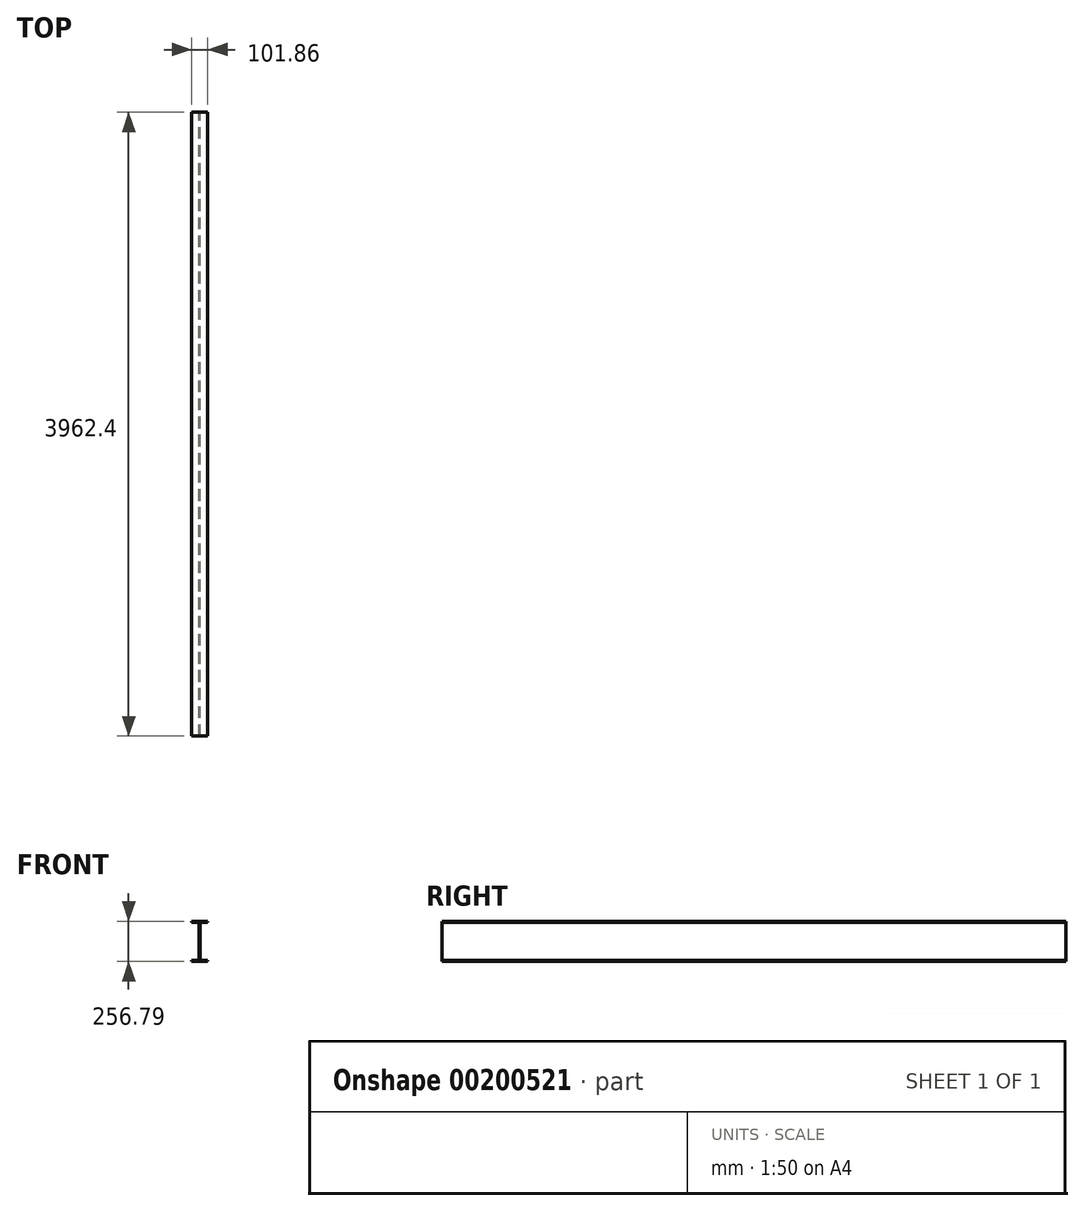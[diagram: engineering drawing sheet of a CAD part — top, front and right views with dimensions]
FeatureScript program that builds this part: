
annotation { "Feature Type Name" : "Feature", "Feature Type Description" : "" }
export const myFeature = defineFeature(function(context is Context, id is Id, definition is map)
    precondition{}
    {
        {
            var Q0;
            Q0=qCreatedBy(makeId("Front.planeOp"),FACE);
            var sketch = newSketch(context, id + "F0", { "sketchPlane" : qUnion([Q0])});
            skLineSegment(sketch, "E0", {"start": v(50.93, 0) * mm, "end": v(50.93, 8.38) * mm});
            skLineSegment(sketch, "E1", {"start": v(50.93, 8.38) * mm, "end": v(3.05, 8.38) * mm});
            skLineSegment(sketch, "E2", {"start": v(3.05, 8.38) * mm, "end": v(3.05, 248.41) * mm});
            skLineSegment(sketch, "E3", {"start": v(3.05, 248.41) * mm, "end": v(50.93, 248.41) * mm});
            skLineSegment(sketch, "E4", {"start": v(50.93, 248.41) * mm, "end": v(50.93, 256.8) * mm});
            skLineSegment(sketch, "E5", {"start": v(50.93, 256.8) * mm, "end": v(0, 256.8) * mm});
            skLineSegment(sketch, "E6", {"start": v(50.93, 0) * mm, "end": v(0, 0) * mm});
            skLineSegment(sketch, "E7", {"start": v(0, -24.07) * mm, "end": v(0, 108.97) * mm, "construction": true});
            skLineSegment(sketch, "E8.MirrorCS", {"start": v(-50.93, 248.41) * mm, "end": v(-50.93, 256.8) * mm});
            skLineSegment(sketch, "E9.MirrorCS", {"start": v(-50.93, 0) * mm, "end": v(-50.93, 8.38) * mm});
            skLineSegment(sketch, "E10.MirrorCS", {"start": v(-50.93, 8.38) * mm, "end": v(-3.05, 8.38) * mm});
            skLineSegment(sketch, "E11.MirrorCS", {"start": v(-3.05, 8.38) * mm, "end": v(-3.05, 248.41) * mm});
            skLineSegment(sketch, "E12.MirrorCS", {"start": v(-3.05, 248.41) * mm, "end": v(-50.93, 248.41) * mm});
            skLineSegment(sketch, "E13.MirrorCS", {"start": v(-50.93, 256.8) * mm, "end": v(0, 256.8) * mm});
            skLineSegment(sketch, "E14.MirrorCS", {"start": v(-50.93, 0) * mm, "end": v(0, 0) * mm});
            skSolve(sketch);
        }
        {
            var Q0;
            Q0=qSketchRegion(id+"F0",true);
            extrude(context, id + "F1", {"entities" : qUnion([Q0]), "depth" : 3962.4 * mm, "offsetDistance" : 25.4 * mm});
        }
    });
